# Revit family: NBS_Senator_MeetingPods_HavenPods_FullHeight_Quad
name_source: partatom
category: Furniture
revit_build: Autodesk Revit 2017 (Build: 20181011_1645(x64)
units: mm (PartAtom-declared; Revit-internal decimal feet)

## family parameters
Always vertical = Yes
Cut with Voids When Loaded = No
Room Calculation Point = No
Shared = No
Work Plane-Based = No

## types (1)
- HAPDQ18
    AssetType = Movable
    BIMObjectName = NBS_Senator_MeetingPods_HavenPods_FullHeightQuad_HAPDQ18
    Category = Pr_40_50_12_53:Meeting pods
    ContrastOuterPanelMaterial = NBS_Concept
    Description = Four person meeting space
    DurationUnit = year
    ExpectedLife = 10
    Features = Internal steel frame with multi layered foam construction , outer vertical panels upholstered in camira blazer fabric (two-tone is standard) , quick release panel connector system , levelling adjusters , integral seat and backrest , optional feature: two-tone upholstery on integrated seat units , accessory: HAPCH coat hanger , accessory: HAPNP name plate, accessory: HAPWBA2 A2 magnetic dry wipe board with hanger, accessory: HAPWBA3 A3 magnetic dry wipe board with hanger,
    FrameMaterial = NBS_Concept
    IfcExportAs = IfcFurnitureType
    IfcExportType = USERDEFINED
    InnerPanelMaterial = NBS_Concept
    IntegralAccessories = Coat hanger, name plate, A2 magnetic dry wipe board with hanger, A3 magnetic dry wipe board with hanger
    IsBuiltIn = No
    ManufacturerName = Senator
    ManufacturerURL = http://www.thesenatorgroup.com
    ModelNumber = HAPDQ18
    ModelReference = Haven Pods Full Height Quad
    NBSCertification = www.nationalbimlibrary.com/cert/cnkmvgyr
    NBSDescription = Meeting pods
    NBSReference = 45-35-20/342
    Name = MeetingPods_HavenPodsFullHeightQuad_HAPDQ18_Senator
    NominalDepth = 2000 mm  [stored 6.56168 ft]
    NominalHeight = 1800 mm  [stored 5.90551 ft]
    NominalLength = 2000 mm  [stored 6.56168 ft]
    NominalWidth = 2000 mm  [stored 6.56168 ft]
    OuterPanelMaterial = NBS_Concept
    ProductInformation = http://www.thesenatorgroup.com
    Size = 2000 x 1800 x 2000 mm
    Status = New
    Style = Workspace pod
    SustainabilityPerformance = http://www.thesenatorgroup.com
    Uniclass2015Code = Pr_40_50_12_53
    Uniclass2015Title = Meeting pods
    Uniclass2015Version = Products v1.12
    Version = 1
    WarrantyDescription = Senator warrants that its manufactured products are free from manufacturing defects - in materials or workmanship - for a period of ten (10) years on Senator seating ranges; and fifteen (15) years on Senator desking ranges
    WarrantyDurationParts = 10
    WarrantyDurationUnit = year

note: [stored X ft] marks values corroborated as IEEE doubles in the binary element streams (Revit-internal decimal feet)

## geometry (parser evidence)
native form markers: Sweep x8
no freeform markers — native parametric forms only
